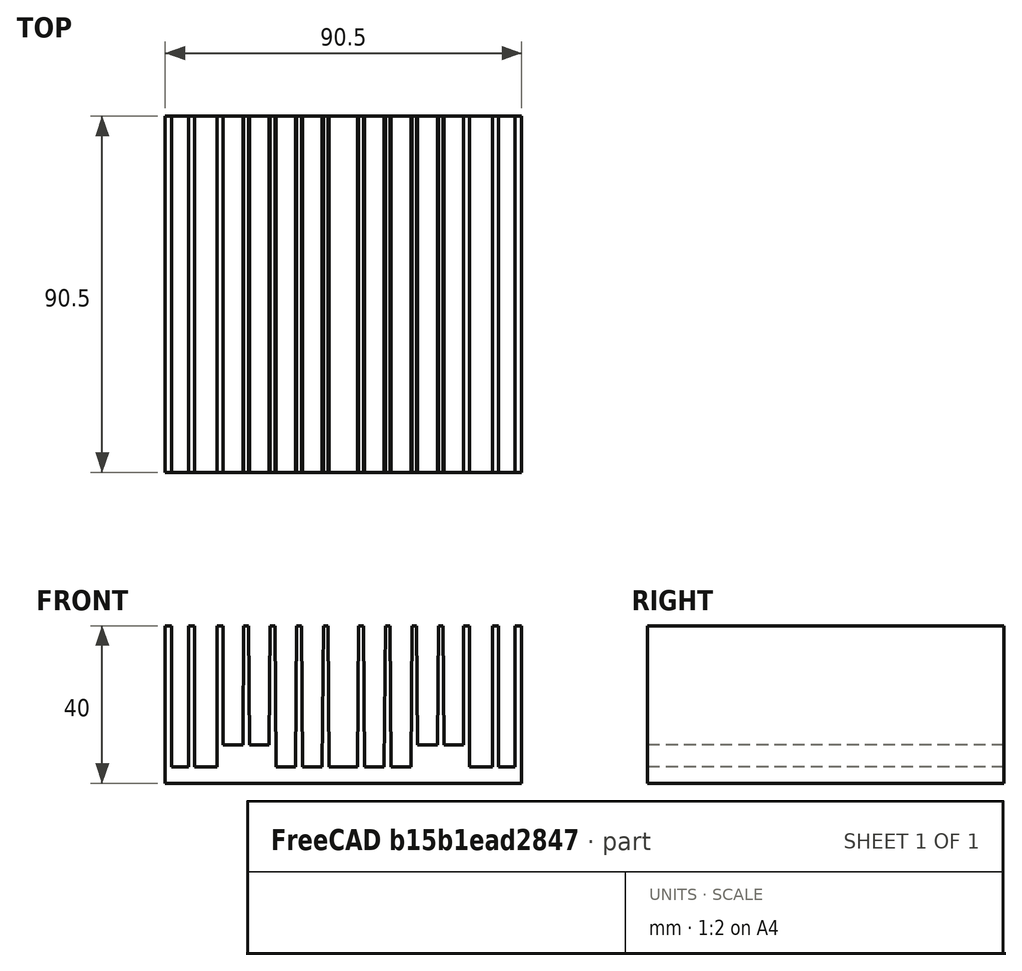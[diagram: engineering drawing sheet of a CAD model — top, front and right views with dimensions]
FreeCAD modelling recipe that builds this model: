
FCSTD DOCUMENT  (FreeCAD 0.19R23634 (Git))
Label: Heatsink_90x90
License: All rights reserved
LicenseURL: http://en.wikipedia.org/wiki/All_rights_reserved
objects: Sketcher::SketchObject×1, PartDesign::Pad×1, PartDesign::Body×1
note: 4 computed .brp shape members not serialized (recipe doc carries the construction recipe); baked Part::Feature solids carry a one-line shape summary decoded from their .brp

FEATURE [Sketcher::SketchObject] Sketch
  FullyConstrained = true
  MapMode = 5
  Placement = pos=(0,0,0) rot=(1,0,0;1.5708rad)
  Support = -> [XZ_Plane]
  sketch-geometry (60):
    g0: LineSegment StartX=-45.25 StartY=0 StartZ=0 EndX=-45.25 EndY=40 EndZ=0
    g1: LineSegment StartX=-45.25 StartY=40 StartZ=0 EndX=-43.65 EndY=40 EndZ=0
    g2: LineSegment StartX=-43.65 StartY=40 StartZ=0 EndX=-43.65 EndY=4.2 EndZ=0
    g3: LineSegment StartX=-43.65 StartY=4.2 StartZ=0 EndX=-39.35 EndY=4.2 EndZ=0
    g4: LineSegment StartX=-39.35 StartY=4.2 StartZ=0 EndX=-39.35 EndY=40 EndZ=0
    g5: LineSegment StartX=-39.35 StartY=40 StartZ=0 EndX=-37.85 EndY=40 EndZ=0
    g6: LineSegment StartX=-37.85 StartY=40 StartZ=0 EndX=-37.85 EndY=4.2 EndZ=0
    g7: LineSegment StartX=-37.85 StartY=4.2 StartZ=0 EndX=-32.05 EndY=4.2 EndZ=0
    g8: LineSegment StartX=-32.05 StartY=4.2 StartZ=0 EndX=-32.05 EndY=40 EndZ=0
    g9: LineSegment StartX=-32.05 StartY=40 StartZ=0 EndX=-30.55 EndY=40 EndZ=0
    g10: LineSegment StartX=-30.55 StartY=40 StartZ=0 EndX=-30.55 EndY=9.8 EndZ=0
    g11: LineSegment StartX=-30.55 StartY=9.8 StartZ=0 EndX=-25.55 EndY=9.8 EndZ=0
    g12: LineSegment StartX=-25.55 StartY=9.8 StartZ=0 EndX=-25.3092 EndY=40 EndZ=0
    g13: LineSegment StartX=-25.3092 StartY=40 StartZ=0 EndX=-24.1092 EndY=40 EndZ=0
    g14: LineSegment StartX=-24.1092 StartY=40 StartZ=0 EndX=-23.8683 EndY=9.8 EndZ=0
    g15: LineSegment StartX=-23.8683 StartY=9.8 StartZ=0 EndX=-18.8683 EndY=9.8 EndZ=0
    g16: LineSegment StartX=-18.8683 StartY=9.8 StartZ=0 EndX=-18.6275 EndY=40 EndZ=0
    g17: LineSegment StartX=-18.6275 StartY=40 StartZ=0 EndX=-17.4275 EndY=40 EndZ=0
    g18: LineSegment StartX=-17.4275 StartY=40 StartZ=0 EndX=-17.142 EndY=4.2 EndZ=0
    g19: LineSegment StartX=-17.142 StartY=4.2 StartZ=0 EndX=-12.142 EndY=4.2 EndZ=0
    g20: LineSegment StartX=-12.142 StartY=4.2 StartZ=0 EndX=-11.8565 EndY=40 EndZ=0
    g21: LineSegment StartX=-11.8565 StartY=40 StartZ=0 EndX=-10.6565 EndY=40 EndZ=0
    g22: LineSegment StartX=-10.6565 StartY=40 StartZ=0 EndX=-10.371 EndY=4.2 EndZ=0
    g23: LineSegment StartX=-10.371 StartY=4.2 StartZ=0 EndX=-5.37099 EndY=4.2 EndZ=0
    g24: LineSegment StartX=-5.37099 StartY=4.2 StartZ=0 EndX=-5.0855 EndY=40 EndZ=0
    g25: LineSegment StartX=-5.0855 StartY=40 StartZ=0 EndX=-3.8855 EndY=40 EndZ=0
    g26: LineSegment StartX=-3.8855 StartY=40 StartZ=0 EndX=-3.6 EndY=4.2 EndZ=0
    g27: LineSegment StartX=-3.6 StartY=4.2 StartZ=0 EndX=3.6 EndY=4.2 EndZ=0
    g28: LineSegment StartX=3.6 StartY=4.2 StartZ=0 EndX=3.8855 EndY=40 EndZ=0
    g29: LineSegment StartX=3.8855 StartY=40 StartZ=0 EndX=5.0855 EndY=40 EndZ=0
    g30: LineSegment StartX=5.0855 StartY=40 StartZ=0 EndX=5.37099 EndY=4.2 EndZ=0
    g31: LineSegment StartX=5.37099 StartY=4.2 StartZ=0 EndX=10.371 EndY=4.2 EndZ=0
    g32: LineSegment StartX=10.371 StartY=4.2 StartZ=0 EndX=10.6565 EndY=40 EndZ=0
    g33: LineSegment StartX=10.6565 StartY=40 StartZ=0 EndX=11.8565 EndY=40 EndZ=0
    g34: LineSegment StartX=11.8565 StartY=40 StartZ=0 EndX=12.142 EndY=4.2 EndZ=0
    g35: LineSegment StartX=12.142 StartY=4.2 StartZ=0 EndX=17.142 EndY=4.2 EndZ=0
    g36: LineSegment StartX=17.142 StartY=4.2 StartZ=0 EndX=17.4275 EndY=40 EndZ=0
    g37: LineSegment StartX=17.4275 StartY=40 StartZ=0 EndX=18.6275 EndY=40 EndZ=0
    g38: LineSegment StartX=18.6275 StartY=40 StartZ=0 EndX=18.8683 EndY=9.8 EndZ=0
    g39: LineSegment StartX=18.8683 StartY=9.8 StartZ=0 EndX=23.8683 EndY=9.8 EndZ=0
    g40: LineSegment StartX=23.8683 StartY=9.8 StartZ=0 EndX=24.1092 EndY=40 EndZ=0
    g41: LineSegment StartX=24.1092 StartY=40 StartZ=0 EndX=25.3092 EndY=40 EndZ=0
    g42: LineSegment StartX=25.3092 StartY=40 StartZ=0 EndX=25.55 EndY=9.8 EndZ=0
    g43: LineSegment StartX=25.55 StartY=9.8 StartZ=0 EndX=30.55 EndY=9.8 EndZ=0
    g44: LineSegment StartX=30.55 StartY=9.8 StartZ=0 EndX=30.55 EndY=40 EndZ=0
    g45: LineSegment StartX=30.55 StartY=40 StartZ=0 EndX=32.05 EndY=40 EndZ=0
    g46: LineSegment StartX=32.05 StartY=40 StartZ=0 EndX=32.05 EndY=4.2 EndZ=0
    g47: LineSegment StartX=32.05 StartY=4.2 StartZ=0 EndX=37.85 EndY=4.2 EndZ=0
    g48: LineSegment StartX=37.85 StartY=4.2 StartZ=0 EndX=37.85 EndY=40 EndZ=0
    g49: LineSegment StartX=37.85 StartY=40 StartZ=0 EndX=39.35 EndY=40 EndZ=0
    g50: LineSegment StartX=39.35 StartY=40 StartZ=0 EndX=39.35 EndY=4.2 EndZ=0
    g51: LineSegment StartX=39.35 StartY=4.2 StartZ=0 EndX=43.65 EndY=4.2 EndZ=0
    g52: LineSegment StartX=43.65 StartY=4.2 StartZ=0 EndX=43.65 EndY=40 EndZ=0
    g53: LineSegment StartX=43.65 StartY=40 StartZ=0 EndX=45.25 EndY=40 EndZ=0
    g54: LineSegment StartX=45.25 StartY=40 StartZ=0 EndX=45.25 EndY=0 EndZ=0
    g55: LineSegment StartX=-24.7092 StartY=42 StartZ=0 EndX=-24.7092 EndY=40 EndZ=0
    g56: LineSegment StartX=-18.0275 StartY=40 StartZ=0 EndX=-18.0275 EndY=42 EndZ=0
    g57: LineSegment StartX=-11.2565 StartY=40 StartZ=0 EndX=-11.2565 EndY=42 EndZ=0
    g58: LineSegment StartX=-4.4855 StartY=40 StartZ=0 EndX=-4.4855 EndY=42 EndZ=0
    g59: LineSegment StartX=-45.25 StartY=0 StartZ=0 EndX=45.25 EndY=0 EndZ=0
  constraints (165):
    c: PointOnObject(g0,g-1)
    c: Vertical(g0)
    c: Coincident(g1,g0)
    c: Coincident(g2,g1)
    c: Vertical(g2)
    c: Coincident(g3,g2)
    c: Horizontal(g3)
    c: Coincident(g4,g3)
    c: Vertical(g4)
    c: Horizontal(g5)
    c: Coincident(g6,g5)
    c: Vertical(g6)
    c: Coincident(g7,g6)
    c: Coincident(g8,g7)
    c: Vertical(g8)
    c: Coincident(g9,g8)
    c: Vertical(g10)
    c: Coincident(g11,g10)
    c: Horizontal(g11)
    c: Coincident(g12,g11)
    c: Coincident(g13,g12)
    c: Horizontal(g13)
    c: Coincident(g15,g14)
    c: Horizontal(g15)
    c: Coincident(g16,g15)
    c: Coincident(g17,g16)
    c: Horizontal(g17)
    c: Coincident(g18,g17)
    c: Coincident(g19,g18)
    c: Coincident(g20,g19)
    c: Coincident(g21,g20)
    c: Horizontal(g21)
    c: Coincident(g22,g21)
    c: Coincident(g23,g22)
    c: Horizontal(g23)
    c: Coincident(g24,g23)
    c: Coincident(g25,g24)
    c: Horizontal(g25)
    c: Coincident(g26,g25)
    c: Coincident(g27,g26)
    c: Coincident(g27,g28)
    c: Coincident(g28,g29)
    c: Horizontal(g29)
    c: Coincident(g29,g30)
    c: Coincident(g30,g31)
    c: Coincident(g31,g32)
    c: Coincident(g32,g33)
    c: Horizontal(g33)
    c: Coincident(g33,g34)
    c: Coincident(g34,g35)
    c: Horizontal(g35)
    c: Coincident(g35,g36)
    c: Coincident(g36,g37)
    c: Horizontal(g37)
    c: Coincident(g37,g38)
    c: Coincident(g38,g39)
    c: Coincident(g39,g40)
    c: Coincident(g40,g41)
    c: Coincident(g41,g42)
    c: Coincident(g42,g43)
    c: Coincident(g43,g44)
    c: Coincident(g44,g45)
    c: Coincident(g45,g46)
    c: Vertical(g46)
    c: Coincident(g46,g47)
    c: Coincident(g47,g48)
    c: Vertical(g48)
    c: Coincident(g48,g49)
    c: Coincident(g49,g50)
    c: Coincident(g50,g51)
    c: Coincident(g51,g52)
    c: Vertical(g52)
    c: Coincident(g52,g53)
    c: Horizontal(g53)
    c: Coincident(g53,g54)
    c: Horizontal(g41)
    c: Horizontal(g45)
    c: Horizontal(g49)
    c: Horizontal(g1)
    c: Symmetric(g0,g54,g-2)
    c: Symmetric(g26,g27,g-2)
    c: DistanceX(g27,g27) = 7.2
    c: Equal(g1,g53)
    c: Equal(g5,g49)
    c: Coincident(g10,g9)
    c: Horizontal(g9)
    c: Equal(g9,g45)
    c: Coincident(g4,g5)
    c: Equal(g41,g13)
    c: Coincident(g14,g13)
    c: Equal(g17,g37)
    c: Equal(g21,g33)
    c: Equal(g25,g29)
    c: Horizontal(g0,g4)
    c: Horizontal(g4,g8)
    c: Horizontal(g8,g12)
    c: Horizontal(g12,g16)
    c: Horizontal(g16,g20)
    c: Horizontal(g20,g24)
    c: Horizontal(g40,g44)
    c: Horizontal(g44,g48)
    c: Horizontal(g48,g52)
    c: Horizontal(g51)
    c: Horizontal(g47)
    c: Horizontal(g43)
    c: Horizontal(g39)
    c: Horizontal(g31)
    c: Horizontal(g19)
    c: Horizontal(g7)
    c: Equal(g51,g3)
    c: Equal(g47,g7)
    c: DistanceX(g1,g1) = 1.6
    c: DistanceX(g3,g3) = 4.3
    c: DistanceX(g7,g7) = 5.8
    c: DistanceX(g9,g9) = 1.5
    c: DistanceX(g5,g5) = 1.5
    c: DistanceX(g13,g13) = 1.2
    c: DistanceX(g17,g17) = 1.2
    c: DistanceX(g21,g21) = 1.2
    c: DistanceX(g25,g25) = 1.2
    c: DistanceX(g23,g23) = 5
    c: DistanceX(g19,g19) = 5
    c: DistanceX(g15,g15) = 5
    c: DistanceX(g11,g11) = 5
    c: Equal(g23,g31)
    c: Equal(g19,g35)
    c: Equal(g15,g39)
    c: Equal(g11,g43)
    c: DistanceX(g0,g54) = 90.5
    c: Symmetric(g28,g25,g-2)
    c: Symmetric(g32,g21,g-2)
    c: Symmetric(g17,g36,g-2)
    c: Symmetric(g40,g13,g-2)
    c: Distance(g55) = 2
    c: PointOnObject(g55,g13)
    c: Symmetric(g12,g13,g55)
    c: Symmetric(g11,g14,g55)
    c: Symmetric(g23,g30,g-2)
    c: Symmetric(g34,g19,g-2)
    c: Symmetric(g15,g38,g-2)
    c: Symmetric(g42,g11,g-2)
    c: Symmetric(g7,g46,g-2)
    c: Symmetric(g50,g3,g-2)
    c: Horizontal(g2,g6)
    c: Horizontal(g6,g18)
    c: DistanceY(g-1,g2) = 4.2
    c: PointOnObject(g56,g17)
    c: Distance(g56) = 2
    c: Symmetric(g16,g17,g56)
    c: PointOnObject(g57,g21)
    c: Distance(g57) = 2
    c: Symmetric(g20,g21,g57)
    c: Symmetric(g22,g19,g57)
    c: PointOnObject(g58,g25)
    c: Distance(g58) = 2
    c: Symmetric(g24,g25,g58)
    c: Symmetric(g26,g23,g58)
    c: DistanceY(g-1,g10) = 9.8
    c: Parallel(g12,g16)
    c: Parallel(g16,g20)
    c: Parallel(g20,g24)
    c: DistanceY(g-1,g0) = 40
    c: Parallel(g14,g18)
    c: Coincident(g59,g0)
    c: Coincident(g59,g54)
FEATURE [PartDesign::Pad] Pad
  Direction = (1,1,1)
  Length = 90.5
  Length2 = 100
  Placement = pos=(0,0,0) rot=(1,0,0;1.5708rad)
  Profile = -> Sketch
  Type = 0
FEATURE [PartDesign::Body] Body  label="Heatsink_Body"
  Group = -> [Sketch,Pad]
  Origin = -> Origin
  Tip = -> Pad
